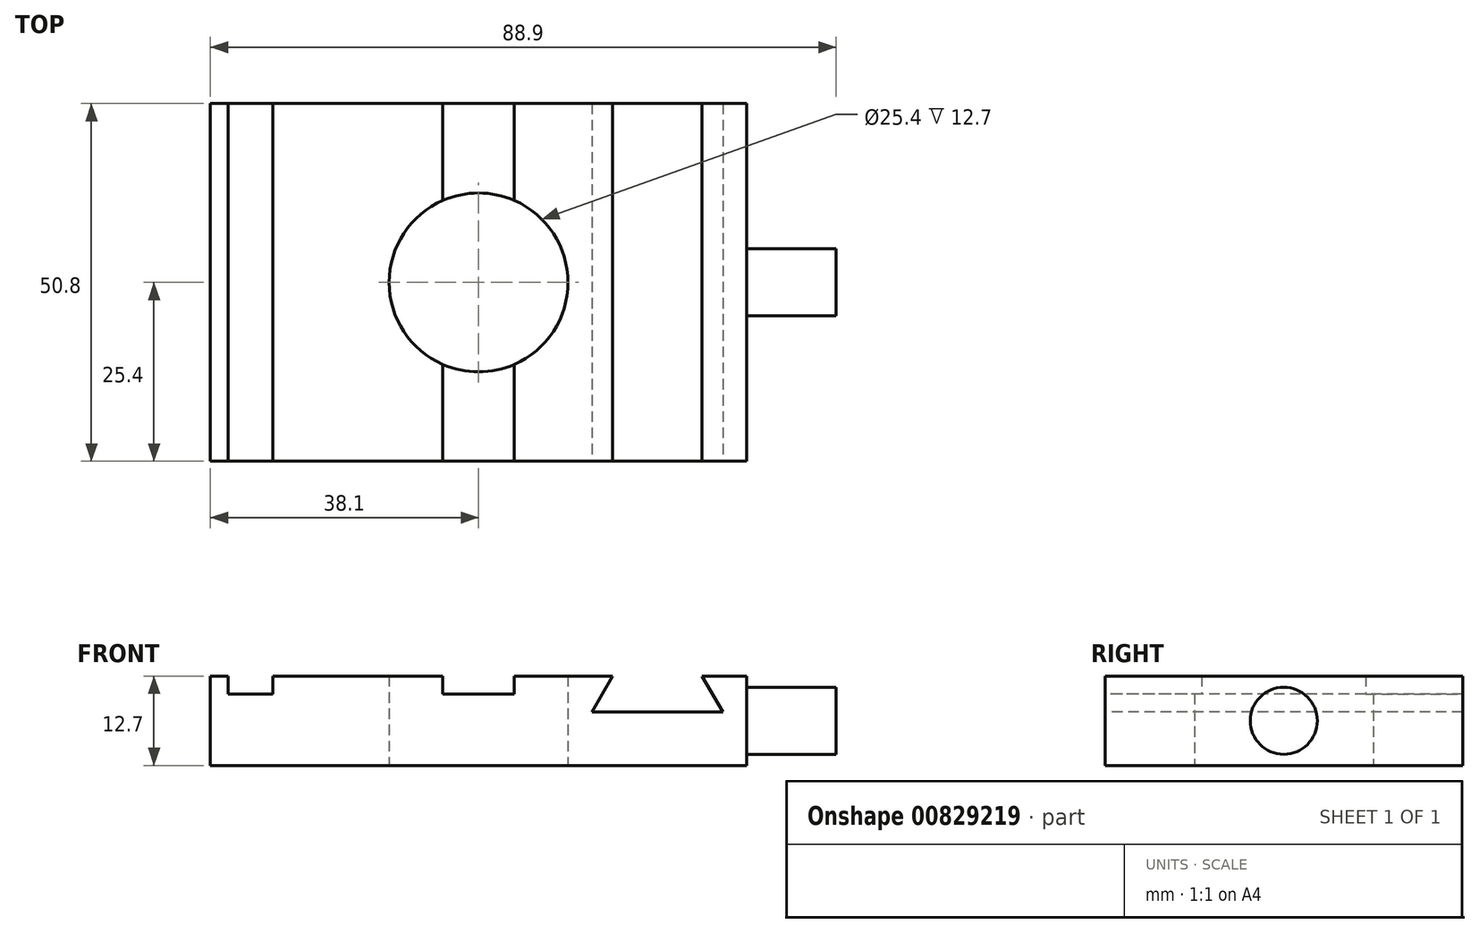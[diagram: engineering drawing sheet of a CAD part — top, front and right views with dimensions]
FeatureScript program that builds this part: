
annotation { "Feature Type Name" : "Feature", "Feature Type Description" : "" }
export const myFeature = defineFeature(function(context is Context, id is Id, definition is map)
    precondition{}
    {
        {
            var Q0;
            Q0=qCreatedBy(makeId("Top.planeOp"),FACE);
            var sketch = newSketch(context, id + "F0", { "sketchPlane" : qUnion([Q0])});
            skLineSegment(sketch, "E0.bottom", {"start": v(38.1, 25.4) * mm, "end": v(-38.1, 25.4) * mm});
            skLineSegment(sketch, "E0.top", {"start": v(38.1, -25.4) * mm, "end": v(-38.1, -25.4) * mm});
            skLineSegment(sketch, "E0.left", {"start": v(38.1, 25.4) * mm, "end": v(38.1, -25.4) * mm});
            skLineSegment(sketch, "E0.right", {"start": v(-38.1, 25.4) * mm, "end": v(-38.1, -25.4) * mm});
            skPoint(sketch, "E0.middle", {"position": v(0, 0) * mm});
            skCircle(sketch, "E1", {"center": v(0, 0) * mm, "radius": 12.7 * mm});
            skSolve(sketch);
        }
        {
            var Q0;
            Q0=makeQuery(id+"F0.imprint","IMPRINT",FACE,{"disambiguationData":[TD([[makeQuery(id+"F0.imprint","IMPRINT",EDGE,{"derivedFrom":sQuery(id+"F0.wireOp",EDGE,"E0.bottom")}),1.0]])]});
            extrude(context, id + "F1", {"entities" : qUnion([Q0]), "depth" : 12.7 * mm, "offsetDistance" : 25.4 * mm});
        }
        {
            var Q0;
            Q0=makeQuery(id+"F1.opExtrude","CAP_FACE",FACE,{"disambiguationData":[OSD([sQuery(id+"F0.wireOp",EDGE,"E0.bottom"),sQuery(id+"F0.wireOp",EDGE,"E0.top"),sQuery(id+"F0.wireOp",EDGE,"E0.left"),sQuery(id+"F0.wireOp",EDGE,"E0.right"),sQuery(id+"F0.wireOp",EDGE,"E1")])],"isStart":false});
            var sketch = newSketch(context, id + "F2", { "sketchPlane" : qUnion([Q0])});
            skLineSegment(sketch, "E2.bottom", {"start": v(-35.56, 25.4) * mm, "end": v(-29.2, 25.4) * mm});
            skLineSegment(sketch, "E2.top", {"start": v(-35.56, -25.4) * mm, "end": v(-29.2, -25.4) * mm});
            skLineSegment(sketch, "E2.left", {"start": v(-35.56, 25.4) * mm, "end": v(-35.56, -25.4) * mm});
            skLineSegment(sketch, "E2.right", {"start": v(-29.2, 25.4) * mm, "end": v(-29.2, -25.4) * mm});
            skLineSegment(sketch, "E3", {"start": v(-5.08, 25.4) * mm, "end": v(-5.08, -25.4) * mm});
            skLineSegment(sketch, "E4", {"start": v(-5.08, -25.4) * mm, "end": v(5.08, -25.4) * mm});
            skLineSegment(sketch, "E5", {"start": v(5.08, -25.4) * mm, "end": v(5.08, 25.4) * mm});
            skLineSegment(sketch, "E6", {"start": v(5.08, 25.4) * mm, "end": v(-5.08, 25.4) * mm});
            skPoint(sketch, "E7", {"position": v(0, 0) * mm});
            skLineSegment(sketch, "E8", {"start": v(0, 25.4) * mm, "end": v(0, -25.4) * mm, "construction": true});
            skSolve(sketch);
        }
        {
            var Q0;
            Q0=makeQuery(id+"F2.imprint","IMPRINT",FACE,{"disambiguationData":[TD([[makeQuery(id+"F2.imprint","IMPRINT",EDGE,{"derivedFrom":sQuery(id+"F2.wireOp",EDGE,"E2.bottom")}),1.0]])]});
            var Q1;
            {var subQ0=sQuery(id+"F2.wireOp",EDGE,"E4");Q1=makeQuery(id+"F2.imprint","IMPRINT",FACE,{"disambiguationData":[TD([[makeQuery(id+"F2.imprint","IMPRINT",EDGE,{"derivedFrom":subQ0}),-1.0]])]});}
            var Q2;
            {var subQ0=sQuery(id+"F2.wireOp",EDGE,"E3");var subQ1=makeQuery(id+"F1.opExtrude","CAP_EDGE",EDGE,{"disambiguationData":[OSD([sQuery(id+"F0.wireOp",EDGE,"E1")])],"isStart":false});var subQ2=makeQuery(id+"F2.imprint","INTERSECT",VERTEX,{"disambiguationData":[OD(0.0)],"derivedFrom":[subQ1,subQ0]});Q2=makeQuery(id+"F2.imprint","IMPRINT",FACE,{"disambiguationData":[TD([[makeQuery(id+"F2.imprint","IMPRINT",EDGE,{"disambiguationData":[TD([[subQ2,-1.0]])],"derivedFrom":subQ0}),1.0]])]});}
            var Q3;
            {var subQ0=sQuery(id+"F2.wireOp",EDGE,"E6");Q3=makeQuery(id+"F2.imprint","IMPRINT",FACE,{"disambiguationData":[TD([[makeQuery(id+"F2.imprint","IMPRINT",EDGE,{"derivedFrom":subQ0}),1.0]])]});}
            extrude(context, id + "F3", {"entities" : qUnion([Q0, Q1, Q2, Q3]), "operationType" : NewBodyOperationType.REMOVE, "oppositeDirection" : true, "depth" : 2.54 * mm, "offsetDistance" : 25.4 * mm});
        }
        {
            var Q0;
            Q0=makeQuery(id+"F1.opExtrude","SWEPT_FACE",FACE,{"disambiguationData":[OSD([sQuery(id+"F0.wireOp",EDGE,"E0.top")])]});
            var sketch = newSketch(context, id + "F4", { "sketchPlane" : qUnion([Q0])});
            skLineSegment(sketch, "E9", {"start": v(19.05, 12.7) * mm, "end": v(16.12, 7.62) * mm});
            skLineSegment(sketch, "E10", {"start": v(16.12, 7.62) * mm, "end": v(34.68, 7.62) * mm});
            skLineSegment(sketch, "E11", {"start": v(34.68, 7.62) * mm, "end": v(31.75, 12.7) * mm});
            skLineSegment(sketch, "E12", {"start": v(31.75, 12.7) * mm, "end": v(19.05, 12.7) * mm});
            skLineSegment(sketch, "E13", {"start": v(25.4, 7.62) * mm, "end": v(25.4, 12.7) * mm, "construction": true});
            skSolve(sketch);
        }
        {
            var Q0;
            Q0=makeQuery(id+"F4.imprint","IMPRINT",FACE,{"disambiguationData":[TD([[makeQuery(id+"F4.imprint","IMPRINT",EDGE,{"derivedFrom":sQuery(id+"F4.wireOp",EDGE,"E9")}),1.0]])]});
            extrude(context, id + "F5", {"entities" : qUnion([Q0]), "operationType" : NewBodyOperationType.REMOVE, "endBound" : BoundingType.THROUGH_ALL, "oppositeDirection" : true, "depth" : 25.4 * mm, "offsetDistance" : 25.4 * mm});
        }
        {
            var Q0;
            Q0=makeQuery(id+"F1.opExtrude","SWEPT_FACE",FACE,{"disambiguationData":[OSD([sQuery(id+"F0.wireOp",EDGE,"E0.left")])]});
            var sketch = newSketch(context, id + "F6", { "sketchPlane" : qUnion([Q0])});
            skCircle(sketch, "E14", {"center": v(0, 6.35) * mm, "radius": 4.76 * mm});
            skPoint(sketch, "E14.centerSnap0", {"position": v(-25.4, 6.35) * mm});
            skPoint(sketch, "E14.centerSnap1", {"position": v(0, 12.7) * mm});
            skSolve(sketch);
        }
        {
            var Q0;
            Q0=makeQuery(id+"F6.imprint","IMPRINT",FACE,{"disambiguationData":[TD([[makeQuery(id+"F6.imprint","IMPRINT",EDGE,{"derivedFrom":sQuery(id+"F6.wireOp",EDGE,"E14")}),1.0]])]});
            extrude(context, id + "F7", {"entities" : qUnion([Q0]), "operationType" : NewBodyOperationType.ADD, "depth" : 12.7 * mm, "offsetDistance" : 25.4 * mm});
        }
    });
